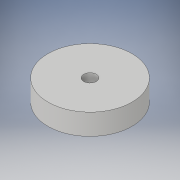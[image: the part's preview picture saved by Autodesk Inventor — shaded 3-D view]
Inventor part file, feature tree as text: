
AUTODESK INVENTOR PART (.ipt)
format: ipt  version: 2019 (Build 230136000, 136)  size: 102,400 bytes
history: native  units: mm
features: sketch x2, other x1, extrude x1, hole x1
ambient origin geometry x8: Origin, YZ Plane, XZ Plane, XY Plane, X Axis, Y Axis, Z Axis, Center Point
bodies: Body1 (feature_tree)
feature tree (5):
  other  "ソリッド1"
  extrude  "押し出し1"  Depth=40.0mm
  hole  "穴1"  [1 undecoded]
  sketch  "スケッチ1"
  sketch  "スケッチ2"
note: 1 required parameter value undecoded (feature->parameter linkage not recoverable at this tier; creation-order binding heuristic only, values carry confidence <= 0.55)
